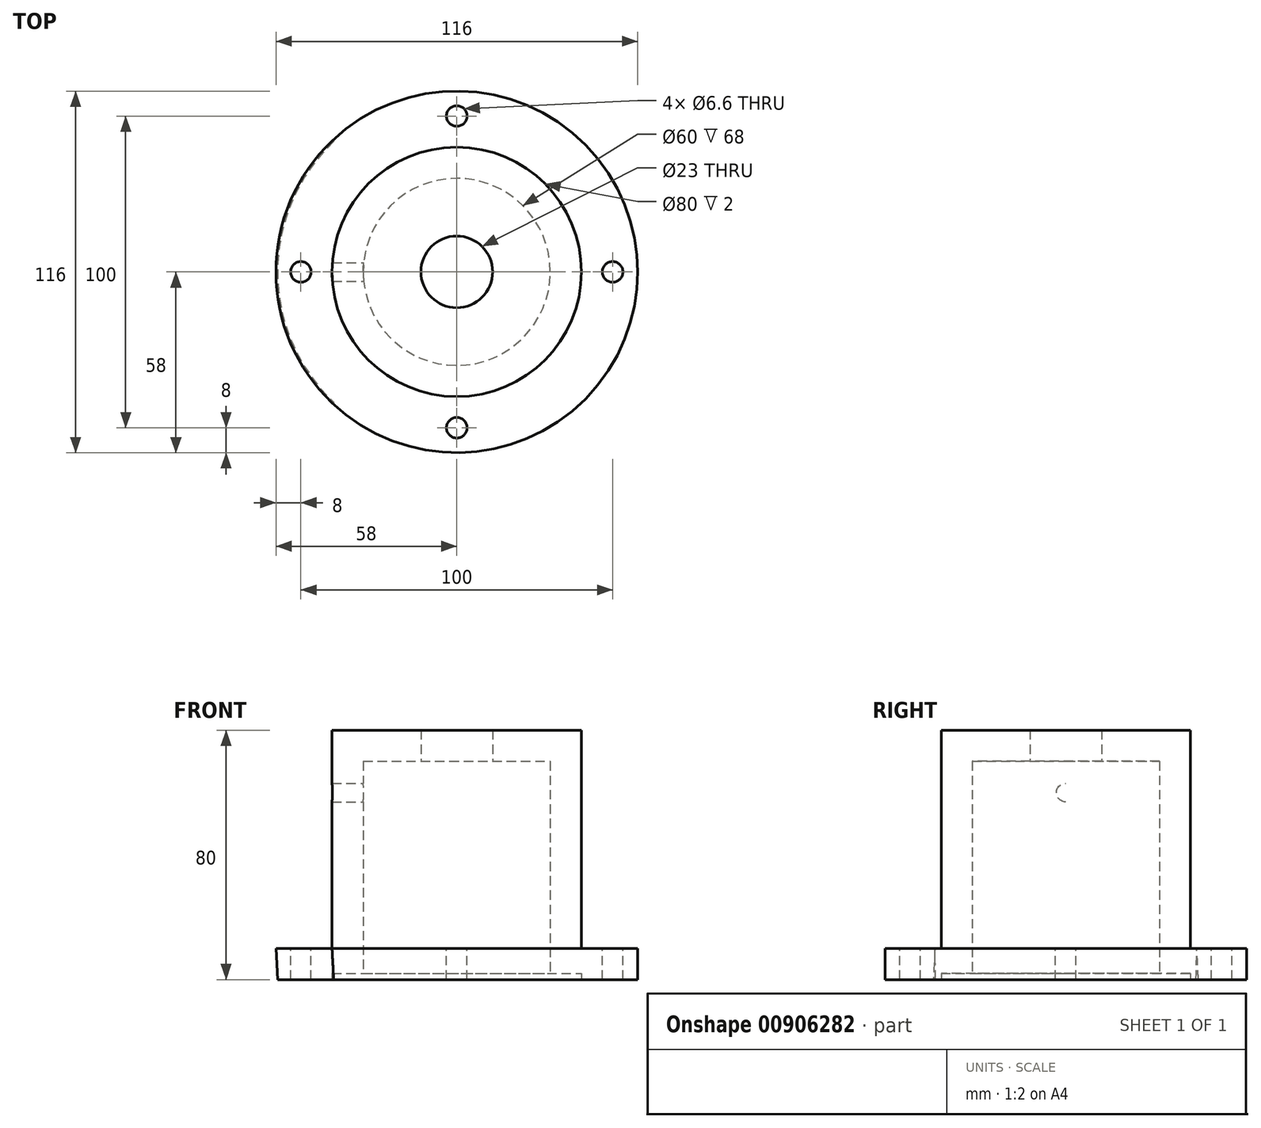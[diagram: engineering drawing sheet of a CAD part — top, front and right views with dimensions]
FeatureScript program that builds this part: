
annotation { "Feature Type Name" : "Feature", "Feature Type Description" : "" }
export const myFeature = defineFeature(function(context is Context, id is Id, definition is map)
    precondition{}
    {
        {
            var Q0;
            Q0=qCreatedBy(makeId("Right.planeOp"),FACE);
            var sketch = newSketch(context, id + "F0", { "sketchPlane" : qUnion([Q0])});
            skLineSegment(sketch, "E0", {"start": v(-30, 2) * mm, "end": v(-40, 2) * mm});
            skLineSegment(sketch, "E1", {"start": v(-40, 2) * mm, "end": v(-40, 0) * mm});
            skLineSegment(sketch, "E2", {"start": v(-40, 0) * mm, "end": v(-58, 0) * mm});
            skLineSegment(sketch, "E3", {"start": v(-58, 0) * mm, "end": v(-58, 10) * mm});
            skLineSegment(sketch, "E4", {"start": v(-58, 10) * mm, "end": v(-40, 10) * mm});
            skLineSegment(sketch, "E5", {"start": v(-40, 10) * mm, "end": v(-40, 80) * mm});
            skLineSegment(sketch, "E6", {"start": v(-40, 80) * mm, "end": v(-11.5, 80) * mm});
            skLineSegment(sketch, "E7", {"start": v(-11.5, 80) * mm, "end": v(-11.5, 70) * mm});
            skLineSegment(sketch, "E8", {"start": v(-11.5, 70) * mm, "end": v(-30, 70) * mm});
            skLineSegment(sketch, "E9", {"start": v(-30, 70) * mm, "end": v(-30, 2) * mm});
            skLineSegment(sketch, "E10", {"start": v(0, 0) * mm, "end": v(0, 49.04) * mm});
            skSolve(sketch);
        }
        {
            var Q0;
            Q0=makeQuery(id+"F0.imprint","IMPRINT",FACE,{"disambiguationData":[TD([[makeQuery(id+"F0.imprint","IMPRINT",EDGE,{"derivedFrom":sQuery(id+"F0.wireOp",EDGE,"E0")}),-1.0]])]});
            var Q1;
            Q1=sQuery(id+"F0.wireOp",EDGE,"E10");
            revolve(context, id + "F1", {"surfaceOperationType" : NewSurfaceOperationType.NEW, "entities" : qUnion([Q0]), "axis" : qUnion([Q1]), "revolveType" : RevolveType.FULL});
        }
        {
            var Q0;
            Q0=makeQuery(id+"F1.opRevolve","SWEPT_FACE",FACE,{"disambiguationData":[OSD([sQuery(id+"F0.wireOp",EDGE,"E4")])]});
            var sketch = newSketch(context, id + "F2", { "sketchPlane" : qUnion([Q0])});
            skPoint(sketch, "E11", {"position": v(-50, 0) * mm});
            skPoint(sketch, "E12.1.0", {"position": v(0, -50) * mm});
            skPoint(sketch, "E12.2.0", {"position": v(50, 0) * mm});
            skPoint(sketch, "E12.3.0", {"position": v(0, 50) * mm});
            skPoint(sketch, "E12.center", {"position": v(0, 0) * mm});
            skSolve(sketch);
        }
        {
            var Q0;
            Q0=sQuery(id+"F2.wireOp",VERTEX,"E11");
            var Q1;
            Q1=sQuery(id+"F2.wireOp",VERTEX,"E12.3.0");
            var Q2;
            Q2=sQuery(id+"F2.wireOp",VERTEX,"E12.2.0");
            var Q3;
            Q3=sQuery(id+"F2.wireOp",VERTEX,"E12.1.0");
            var Q4;
            Q4=makeQuery(id+"F1.opRevolve","SWEPT_BODY",BODY,{"disambiguationData":[OSD([sQuery(id+"F0.wireOp",EDGE,"E0"),sQuery(id+"F0.wireOp",EDGE,"E1"),sQuery(id+"F0.wireOp",EDGE,"E2"),sQuery(id+"F0.wireOp",EDGE,"E3"),sQuery(id+"F0.wireOp",EDGE,"E4"),sQuery(id+"F0.wireOp",EDGE,"E5"),sQuery(id+"F0.wireOp",EDGE,"E6"),sQuery(id+"F0.wireOp",EDGE,"E7"),sQuery(id+"F0.wireOp",EDGE,"E8"),sQuery(id+"F0.wireOp",EDGE,"E9")])]});
            hole(context, id + "F3", {"style" : HoleStyle.SIMPLE, "endStyle" : HoleEndStyle.THROUGH, "standardTappedOrClearance" : lookupTablePath({ "fit" : "Normal", "standard" : "ISO", "size" : "M6", "type" : "Clearance" }), "standardBlindInLast" : lookupTablePath({ "fit" : "Normal", "standard" : "ISO", "size" : "M6", "type" : "Clearance" }), "holeDiameter" : 6.6 * mm, "majorDiameter" : 5 * mm, "isTappedThrough" : true, "tappedDepth" : 12 * mm, "tapClearance" : 3, "locations" : qUnion([Q0, Q1, Q2, Q3]), "scope" : qUnion([Q4])});
        }
        {
            var Q0;
            Q0=qCreatedBy(makeId("Right.planeOp"),FACE);
            var sketch = newSketch(context, id + "F4", { "sketchPlane" : qUnion([Q0])});
            skPoint(sketch, "E13", {"position": v(0, 60) * mm});
            skSolve(sketch);
        }
        {
            var Q0;
            Q0=sQuery(id+"F4.wireOp",VERTEX,"E13");
            var Q1;
            Q1=makeQuery(id+"F1.opRevolve","SWEPT_BODY",BODY,{"disambiguationData":[OSD([sQuery(id+"F0.wireOp",EDGE,"E0"),sQuery(id+"F0.wireOp",EDGE,"E1"),sQuery(id+"F0.wireOp",EDGE,"E2"),sQuery(id+"F0.wireOp",EDGE,"E3"),sQuery(id+"F0.wireOp",EDGE,"E4"),sQuery(id+"F0.wireOp",EDGE,"E5"),sQuery(id+"F0.wireOp",EDGE,"E6"),sQuery(id+"F0.wireOp",EDGE,"E7"),sQuery(id+"F0.wireOp",EDGE,"E8"),sQuery(id+"F0.wireOp",EDGE,"E9")])]});
            hole(context, id + "F5", {"style" : HoleStyle.SIMPLE, "endStyle" : HoleEndStyle.THROUGH, "holeDiameter" : 6 * mm, "majorDiameter" : 5 * mm, "isTappedThrough" : true, "tappedDepth" : 12 * mm, "tapClearance" : 3, "locations" : qUnion([Q0]), "scope" : qUnion([Q1])});
        }
        {
            var Q0;
            Q0=makeQuery(id+"F1.opRevolve","SWEPT_FACE",FACE,{"disambiguationData":[OSD([sQuery(id+"F0.wireOp",EDGE,"E4")])]});
            var sketch = newSketch(context, id + "F6", { "sketchPlane" : qUnion([Q0])});
            skLineSegment(sketch, "E14.bottom", {"start": v(-40, 0) * mm, "end": v(-65.59, 0) * mm});
            skLineSegment(sketch, "E14.top", {"start": v(-40, 47.56) * mm, "end": v(-65.59, 47.56) * mm});
            skLineSegment(sketch, "E14.left", {"start": v(-40, 0) * mm, "end": v(-40, 47.56) * mm});
            skLineSegment(sketch, "E14.right", {"start": v(-65.59, 0) * mm, "end": v(-65.59, 47.56) * mm});
            skLineSegment(sketch, "E15.bottom", {"start": v(-40, 0) * mm, "end": v(-65.82, 0) * mm});
            skLineSegment(sketch, "E15.top", {"start": v(-40, -53.25) * mm, "end": v(-65.82, -53.25) * mm});
            skLineSegment(sketch, "E15.left", {"start": v(-40, 0) * mm, "end": v(-40, -53.25) * mm});
            skLineSegment(sketch, "E15.right", {"start": v(-65.82, 0) * mm, "end": v(-65.82, -53.25) * mm});
            skSolve(sketch);
        }
        {
            var Q0;
            {var subQ1=sQuery(id+"F6.wireOp",EDGE,"E15.bottom");var subQ6=makeQuery(id+"F3.hole-0.boolean.opBoolean","COPY",EDGE,{"derivedFrom":makeQuery(id+"F3.hole-0.opRevolve","SWEPT_EDGE",EDGE,{"disambiguationData":[OSD([sQuery(id+"F3.hole-0.sketch.wireOp",EDGE,"core_line_2"),sQuery(id+"F3.hole-0.sketch.wireOp",EDGE,"core_line_3")])]})});var subQ8=makeQuery(id+"F6.imprint","INTERSECT",VERTEX,{"disambiguationData":[OD(1.0)],"derivedFrom":[subQ6,subQ1]});Q0=makeQuery(id+"F6.imprint","IMPRINT",FACE,{"disambiguationData":[TD([[makeQuery(id+"F6.imprint","IMPRINT",EDGE,{"disambiguationData":[TD([[subQ8,-1.0]])],"derivedFrom":subQ1}),1.0]])]});}
            var Q1;
            {var subQ1=sQuery(id+"F6.wireOp",EDGE,"E15.top");Q1=makeQuery(id+"F6.imprint","IMPRINT",FACE,{"disambiguationData":[TD([[makeQuery(id+"F6.imprint","IMPRINT",EDGE,{"derivedFrom":subQ1}),-1.0]])]});}
            var Q2;
            {var subQ4=sQuery(id+"F6.wireOp",EDGE,"E15.bottom");var subQ7=makeQuery(id+"F3.hole-0.boolean.opBoolean","COPY",EDGE,{"derivedFrom":makeQuery(id+"F3.hole-0.opRevolve","SWEPT_EDGE",EDGE,{"disambiguationData":[OSD([sQuery(id+"F3.hole-0.sketch.wireOp",EDGE,"core_line_2"),sQuery(id+"F3.hole-0.sketch.wireOp",EDGE,"core_line_3")])]})});var subQ9=makeQuery(id+"F6.imprint","INTERSECT",VERTEX,{"disambiguationData":[OD(1.0)],"derivedFrom":[subQ7,subQ4]});Q2=makeQuery(id+"F6.imprint","IMPRINT",FACE,{"disambiguationData":[TD([[makeQuery(id+"F6.imprint","IMPRINT",EDGE,{"disambiguationData":[TD([[subQ9,-1.0]])],"derivedFrom":subQ4}),-1.0]])]});}
            var Q3;
            {var subQ6=sQuery(id+"F6.wireOp",EDGE,"E14.top");Q3=makeQuery(id+"F6.imprint","IMPRINT",FACE,{"disambiguationData":[TD([[makeQuery(id+"F6.imprint","IMPRINT",EDGE,{"derivedFrom":subQ6}),1.0]])]});}
            extrude(context, id + "F7", {"entities" : qUnion([Q0, Q1, Q2, Q3]), "operationType" : NewBodyOperationType.REMOVE, "oppositeDirection" : true, "depth" : 66 * mm, "offsetDistance" : 25 * mm, "hasDraft" : true, "draftAngle" : 3 * degree});
        }
    });
